# Revit family: Fireplace_Gas_DaVinci_Linear-SS
name_source: partatom
category: Mechanical Equipment
units: mm (PartAtom-declared; Revit-internal decimal feet)

## family parameters
Classification Number = 23.40.20.34.14
Cut with Voids When Loaded = No
Host = Face
Maintain Annotation Orientation = No
Part Type = Normal
Room Calculation Point = No
Round Connector Dimension = Use Diameter
Shared = No

## types (1)
- Fireplace_Gas_DaVinci_Linear-SS
    Assembly Code = E1090900
    BTU Input Notes = BTU Input per linear foot of the Fireplace Length
    BTU Input per Foot = 3
    Construction Details = http://www.arcat.com
    Default Elevation = 0' - 0"
    Electrical_Amperage = 7 A
    Electrical_Voltage = 120 V
    Expected Lifespan (Years) = 0
    HVAC_BTU Input = 43500.0 Btu/h
    Keynote = 10 31 00
    Locate Air Inlet A = 0' - 4 29/32"
    Locate Air Inlet B = 0' - 7 11/32"
    Locate Air Inlet C = 1' - 1 3/4"
    Locate Air Inlet D = 0' - 7 1/4"
    Locate Exhaust = 1' - 7"
    Maintenance Schedule (Months) = 0
    Manufacturer = DaVinci Custom Fireplaces , Travis Industries Division
    Manufacturer Fax = 425-609-2781
    Manufacturer Website = http://www.davincifireplace.com
    Model = As Specified
    Opening Height = 2' - 6"
    Opening Height from Base of Unit = 0' - 11 1/8"
    Opening Length = 3' - 0"
    Product Data = http://www.arcat.com
    Product Properties = http://www.davincifireplace.com
    Revision = R1_2017-04
    Sales Information = http://www.davincifireplace.com
    SpecWizard = http://www.arcat.com
    Specification = http://www.arcat.com
    Standards Conformance = as Specified
    URL = http://www.davincifireplace.com
    Unit Depth = 1' - 7 5/8"
    Unit Height = 4' - 11 3/16"
    Unit Length = 3' - 2"
    Warranty Duration (Years) = 0

## geometry (parser evidence)
native form markers: Sweep x2
no freeform markers — native parametric forms only
